# Revit family: 1Freestanding Tub Filler_TOTO_TBG09306
name_source: partatom
category: 衛生器具
revit_build: Autodesk Revit 2018 (Build: 20170223_1515(x64)
units: mm (PartAtom-declared; Revit-internal decimal feet)

## family parameters
OmniClass タイトル = Sanitary, Laundry, and Cleaning Equipment
OmniClass 番号 = 23.45.00.00
パーツ タイプ = 標準
ロード時にボイドで切り取り = いいえ
丸型コネクタ寸法 = 直径を使用
作業面ベース = いいえ
共有 = いいえ
常に垂直 = はい
部屋計算ポイント = いいえ

## types (1)
- 1Freestanding Tub Filler_TOTO_TBG09306
    Finish = faucet_material
    Height = 922
    Length = 364.8
    Width = 136.9  [stored 0.449147 ft]
    タイプの説明 = Required Freestanding Tub Filler Base(TBN01105B)/水嘴固定配件(TBN01105B)需另购*TOTO USA:TBN01105U
    排気配管 = いいえ
    排水配管 = はい
    水配管 = はい
    温水配管 = はい
    製造元 = TOTO Ltd.
    説明 = Freestanding Tub Filler/立式单柄双控浴缸水嘴(带手持花洒)

note: [stored X ft] marks values corroborated as IEEE doubles in the binary element streams (Revit-internal decimal feet)

## geometry (parser evidence)
native form markers: Sweep x2
no freeform markers — native parametric forms only
